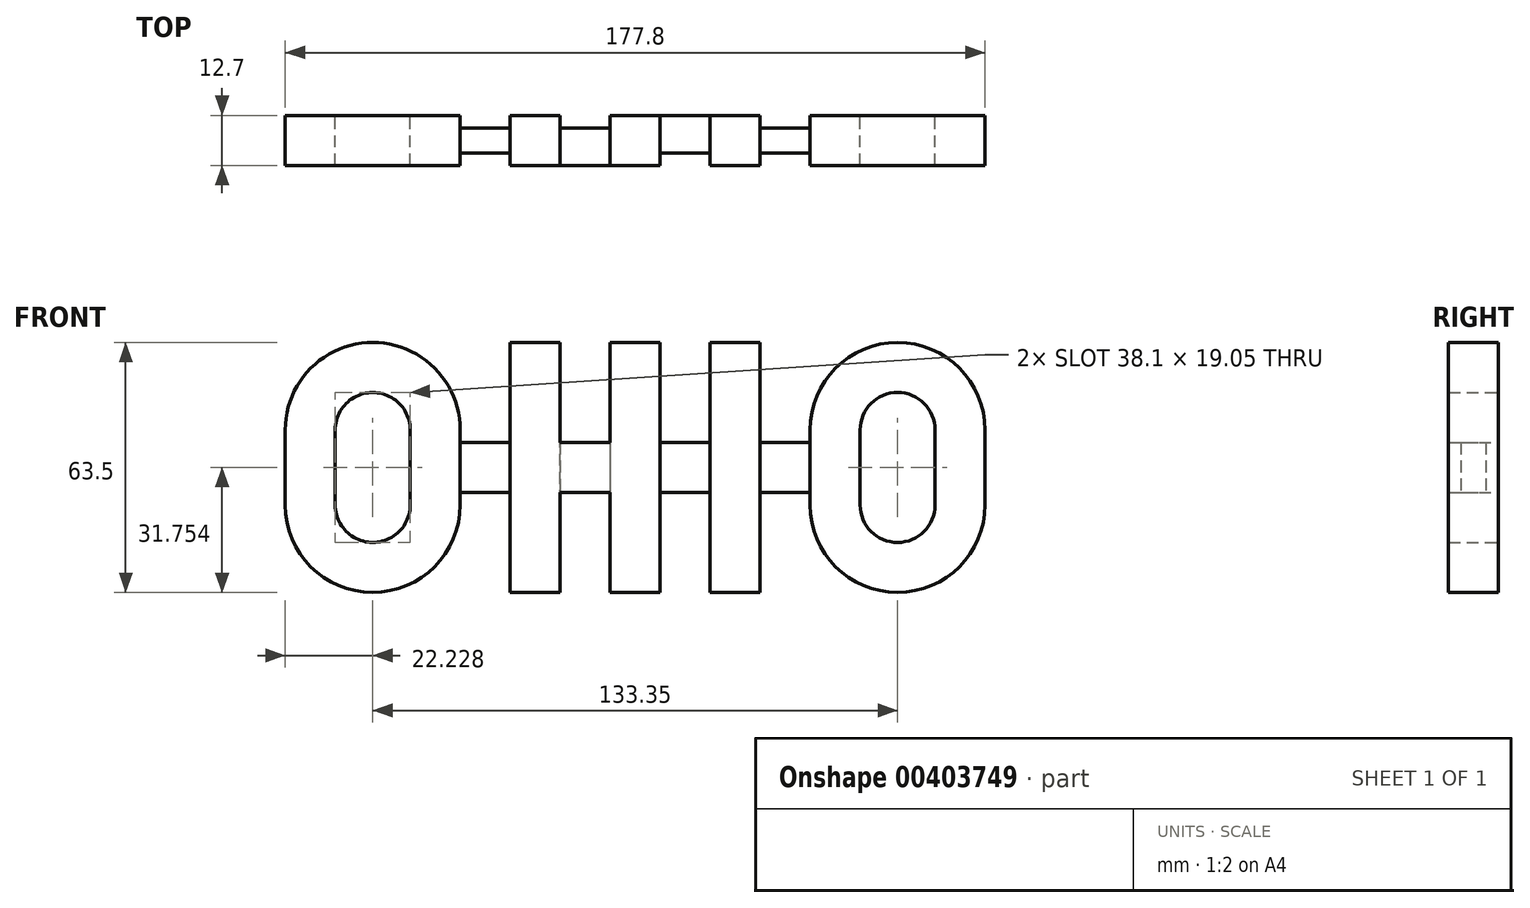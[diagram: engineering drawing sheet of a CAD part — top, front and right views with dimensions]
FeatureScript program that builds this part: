
annotation { "Feature Type Name" : "Feature", "Feature Type Description" : "" }
export const myFeature = defineFeature(function(context is Context, id is Id, definition is map)
    precondition{}
    {
        {
            var Q0;
            Q0=qCreatedBy(makeId("Front.planeOp"),FACE);
            var sketch = newSketch(context, id + "F0", { "sketchPlane" : qUnion([Q0])});
            skLineSegment(sketch, "E0", {"start": v(-86.55, 35.25) * mm, "end": v(-86.55, 16.2) * mm});
            skLineSegment(sketch, "E1", {"start": v(-42.1, 35.25) * mm, "end": v(-42.1, 16.2) * mm});
            skArc(sketch, "E2", {"start": v(-86.55, 35.25) * mm, "mid": v(-64.32, 57.47) * mm, "end": v(-42.1, 35.25) * mm});
            skArc(sketch, "E3", {"start": v(-86.55, 16.2) * mm, "mid": v(-64.32, -6.03) * mm, "end": v(-42.1, 16.2) * mm});
            skArc(sketch, "E4.0", {"start": v(-73.85, 35.25) * mm, "mid": v(-64.32, 44.77) * mm, "end": v(-54.8, 35.25) * mm});
            skLineSegment(sketch, "E4.1", {"start": v(-73.85, 35.25) * mm, "end": v(-73.85, 16.2) * mm});
            skArc(sketch, "E4.2", {"start": v(-73.85, 16.2) * mm, "mid": v(-64.32, 6.67) * mm, "end": v(-54.8, 16.2) * mm});
            skLineSegment(sketch, "E4.3", {"start": v(-54.8, 35.25) * mm, "end": v(-54.8, 16.2) * mm});
            skLineSegment(sketch, "E5", {"start": v(-29.4, 57.47) * mm, "end": v(-29.4, -6.03) * mm});
            skLineSegment(sketch, "E6", {"start": v(-29.4, -6.03) * mm, "end": v(-16.7, -6.03) * mm});
            skLineSegment(sketch, "E7", {"start": v(-16.7, -6.03) * mm, "end": v(-16.7, 19.37) * mm});
            skLineSegment(sketch, "E8", {"start": v(-4, 19.37) * mm, "end": v(-4, -6.03) * mm});
            skLineSegment(sketch, "E9", {"start": v(-4, -6.03) * mm, "end": v(8.7, -6.03) * mm});
            skLineSegment(sketch, "E10", {"start": v(8.7, -6.03) * mm, "end": v(8.7, 57.47) * mm});
            skLineSegment(sketch, "E11", {"start": v(8.7, 57.47) * mm, "end": v(-4, 57.47) * mm});
            skLineSegment(sketch, "E12", {"start": v(-4, 57.47) * mm, "end": v(-4, 32.07) * mm});
            skLineSegment(sketch, "E13", {"start": v(-16.7, 32.07) * mm, "end": v(-16.7, 57.47) * mm});
            skLineSegment(sketch, "E14", {"start": v(-16.7, 57.47) * mm, "end": v(-29.4, 57.47) * mm});
            skLineSegment(sketch, "E15", {"start": v(-42.1, 25.72) * mm, "end": v(-29.4, 25.72) * mm, "construction": true});
            skLineSegment(sketch, "E16.bottom", {"start": v(21.4, 57.47) * mm, "end": v(34.1, 57.47) * mm});
            skLineSegment(sketch, "E16.top", {"start": v(21.4, -6.03) * mm, "end": v(34.1, -6.03) * mm});
            skLineSegment(sketch, "E16.left", {"start": v(21.4, 57.47) * mm, "end": v(21.4, -6.03) * mm});
            skLineSegment(sketch, "E16.right", {"start": v(34.1, 57.47) * mm, "end": v(34.1, -6.03) * mm});
            skLineSegment(sketch, "E17", {"start": v(8.7, 25.72) * mm, "end": v(21.4, 25.72) * mm, "construction": true});
            skLineSegment(sketch, "E18", {"start": v(46.8, 35.25) * mm, "end": v(46.8, 16.2) * mm});
            skLineSegment(sketch, "E19", {"start": v(91.25, 35.25) * mm, "end": v(91.25, 16.2) * mm});
            skArc(sketch, "E20", {"start": v(46.8, 35.25) * mm, "mid": v(69.03, 57.47) * mm, "end": v(91.25, 35.25) * mm});
            skArc(sketch, "E21", {"start": v(46.8, 16.2) * mm, "mid": v(69.03, -6.03) * mm, "end": v(91.25, 16.2) * mm});
            skArc(sketch, "E22.0", {"start": v(59.5, 35.25) * mm, "mid": v(69.03, 44.77) * mm, "end": v(78.55, 35.25) * mm});
            skLineSegment(sketch, "E22.1", {"start": v(59.5, 35.25) * mm, "end": v(59.5, 16.2) * mm});
            skArc(sketch, "E22.2", {"start": v(59.5, 16.2) * mm, "mid": v(69.03, 6.67) * mm, "end": v(78.55, 16.2) * mm});
            skLineSegment(sketch, "E22.3", {"start": v(78.55, 35.25) * mm, "end": v(78.55, 16.2) * mm});
            skLineSegment(sketch, "E23", {"start": v(34.1, 25.72) * mm, "end": v(46.8, 25.72) * mm, "construction": true});
            skLineSegment(sketch, "E24", {"start": v(-64.32, -6.03) * mm, "end": v(-60.84, -5.75) * mm, "construction": true});
            skLineSegment(sketch, "E25", {"start": v(-64.32, -6.03) * mm, "end": v(69.03, -6.03) * mm, "construction": true});
            skLineSegment(sketch, "E26", {"start": v(-4, 32.07) * mm, "end": v(-4, 19.37) * mm});
            skLineSegment(sketch, "E27", {"start": v(-16.7, 32.07) * mm, "end": v(-16.7, 19.37) * mm});
            skSolve(sketch);
        }
        {
            var Q0;
            Q0=makeQuery(id+"F0.imprint","IMPRINT",FACE,{"disambiguationData":[TD([[makeQuery(id+"F0.imprint","IMPRINT",EDGE,{"derivedFrom":sQuery(id+"F0.wireOp",EDGE,"E0")}),1.0]])]});
            var sketch = newSketch(context, id + "F1", { "sketchPlane" : qUnion([Q0])});
            skLineSegment(sketch, "E28.bottom", {"start": v(-29.4, 32.07) * mm, "end": v(-42.1, 32.07) * mm});
            skLineSegment(sketch, "E28.top", {"start": v(-29.4, 19.37) * mm, "end": v(-42.1, 19.37) * mm});
            skLineSegment(sketch, "E28.left", {"start": v(-29.4, 32.07) * mm, "end": v(-29.4, 19.37) * mm});
            skLineSegment(sketch, "E28.right", {"start": v(-42.1, 32.07) * mm, "end": v(-42.1, 19.37) * mm});
            skLineSegment(sketch, "E29.bottom", {"start": v(21.4, 32.07) * mm, "end": v(8.7, 32.07) * mm});
            skLineSegment(sketch, "E29.top", {"start": v(21.4, 19.37) * mm, "end": v(8.7, 19.37) * mm});
            skLineSegment(sketch, "E29.left", {"start": v(21.4, 32.07) * mm, "end": v(21.4, 19.37) * mm});
            skLineSegment(sketch, "E29.right", {"start": v(8.7, 32.07) * mm, "end": v(8.7, 19.37) * mm});
            skLineSegment(sketch, "E30", {"start": v(167.45, 25.72) * mm, "end": v(-73.85, 25.72) * mm, "construction": true});
            skPoint(sketch, "E30.endSnap0", {"position": v(15.05, 25.72) * mm});
            skLineSegment(sketch, "E31.bottom", {"start": v(46.8, 32.07) * mm, "end": v(34.1, 32.07) * mm});
            skLineSegment(sketch, "E31.top", {"start": v(46.8, 19.37) * mm, "end": v(34.1, 19.37) * mm});
            skLineSegment(sketch, "E31.left", {"start": v(46.8, 32.07) * mm, "end": v(46.8, 19.37) * mm});
            skLineSegment(sketch, "E31.right", {"start": v(34.1, 32.07) * mm, "end": v(34.1, 19.37) * mm});
            skLineSegment(sketch, "E32.bottom", {"start": v(-16.7, 32.03) * mm, "end": v(-4, 32.03) * mm});
            skLineSegment(sketch, "E32.top", {"start": v(-16.7, 19.33) * mm, "end": v(-4, 19.33) * mm});
            skLineSegment(sketch, "E32.left", {"start": v(-16.7, 32.03) * mm, "end": v(-16.7, 19.33) * mm});
            skLineSegment(sketch, "E32.right", {"start": v(-4, 32.03) * mm, "end": v(-4, 19.33) * mm});
            skLineSegment(sketch, "E33", {"start": v(-86.26, 23.28) * mm, "end": v(91.54, 23.28) * mm, "construction": true});
            skSolve(sketch);
        }
        {
            var Q0;
            Q0=makeQuery(id+"F1.imprint","IMPRINT",FACE,{"disambiguationData":[TD([[makeQuery(id+"F1.imprint","IMPRINT",EDGE,{"derivedFrom":sQuery(id+"F1.wireOp",EDGE,"E31.bottom")}),1.0]])]});
            var Q1;
            Q1=makeQuery(id+"F1.imprint","IMPRINT",FACE,{"disambiguationData":[TD([[makeQuery(id+"F1.imprint","IMPRINT",EDGE,{"derivedFrom":sQuery(id+"F1.wireOp",EDGE,"E28.bottom")}),1.0]])]});
            extrude(context, id + "F2", {"entities" : qUnion([Q0, Q1]), "depth" : 9.52 * mm, "hasSecondDirection" : true, "secondDirectionOppositeDirection" : true, "secondDirectionDepth" : -3.17 * mm});
        }
        {
            var Q0;
            Q0=makeQuery(id+"F1.imprint","IMPRINT",FACE,{"disambiguationData":[TD([[makeQuery(id+"F1.imprint","IMPRINT",EDGE,{"derivedFrom":sQuery(id+"F1.wireOp",EDGE,"E29.bottom")}),1.0]])]});
            extrude(context, id + "F3", {"entities" : qUnion([Q0]), "operationType" : NewBodyOperationType.ADD, "depth" : 9.52 * mm});
        }
        {
            var Q0;
            Q0=makeQuery(id+"F0.imprint","IMPRINT",FACE,{"disambiguationData":[TD([[makeQuery(id+"F0.imprint","IMPRINT",EDGE,{"derivedFrom":sQuery(id+"F0.wireOp",EDGE,"E0")}),1.0]])]});
            var Q1;
            Q1=makeQuery(id+"F0.imprint","IMPRINT",FACE,{"disambiguationData":[TD([[makeQuery(id+"F0.imprint","IMPRINT",EDGE,{"derivedFrom":sQuery(id+"F0.wireOp",EDGE,"E5")}),1.0]])]});
            var Q2;
            Q2=makeQuery(id+"F0.imprint","IMPRINT",FACE,{"disambiguationData":[TD([[makeQuery(id+"F0.imprint","IMPRINT",EDGE,{"derivedFrom":sQuery(id+"F0.wireOp",EDGE,"E8")}),1.0]])]});
            var Q3;
            Q3=makeQuery(id+"F0.imprint","IMPRINT",FACE,{"disambiguationData":[TD([[makeQuery(id+"F0.imprint","IMPRINT",EDGE,{"derivedFrom":sQuery(id+"F0.wireOp",EDGE,"E16.bottom")}),-1.0]])]});
            var Q4;
            Q4=makeQuery(id+"F0.imprint","IMPRINT",FACE,{"disambiguationData":[TD([[makeQuery(id+"F0.imprint","IMPRINT",EDGE,{"derivedFrom":sQuery(id+"F0.wireOp",EDGE,"E18")}),1.0]])]});
            extrude(context, id + "F4", {"entities" : qUnion([Q0, Q1, Q2, Q3, Q4]), "operationType" : NewBodyOperationType.ADD, "depth" : 12.7 * mm});
        }
        {
            var Q0;
            Q0=makeQuery(id+"F1.imprint","IMPRINT",FACE,{"disambiguationData":[TD([[makeQuery(id+"F1.imprint","IMPRINT",EDGE,{"derivedFrom":sQuery(id+"F1.wireOp",EDGE,"E32.bottom")}),-1.0]])]});
            extrude(context, id + "F5", {"entities" : qUnion([Q0]), "operationType" : NewBodyOperationType.ADD, "depth" : 12.7 * mm, "hasSecondDirection" : true, "secondDirectionOppositeDirection" : false, "secondDirectionDepth" : 3.17 * mm});
        }
    });
